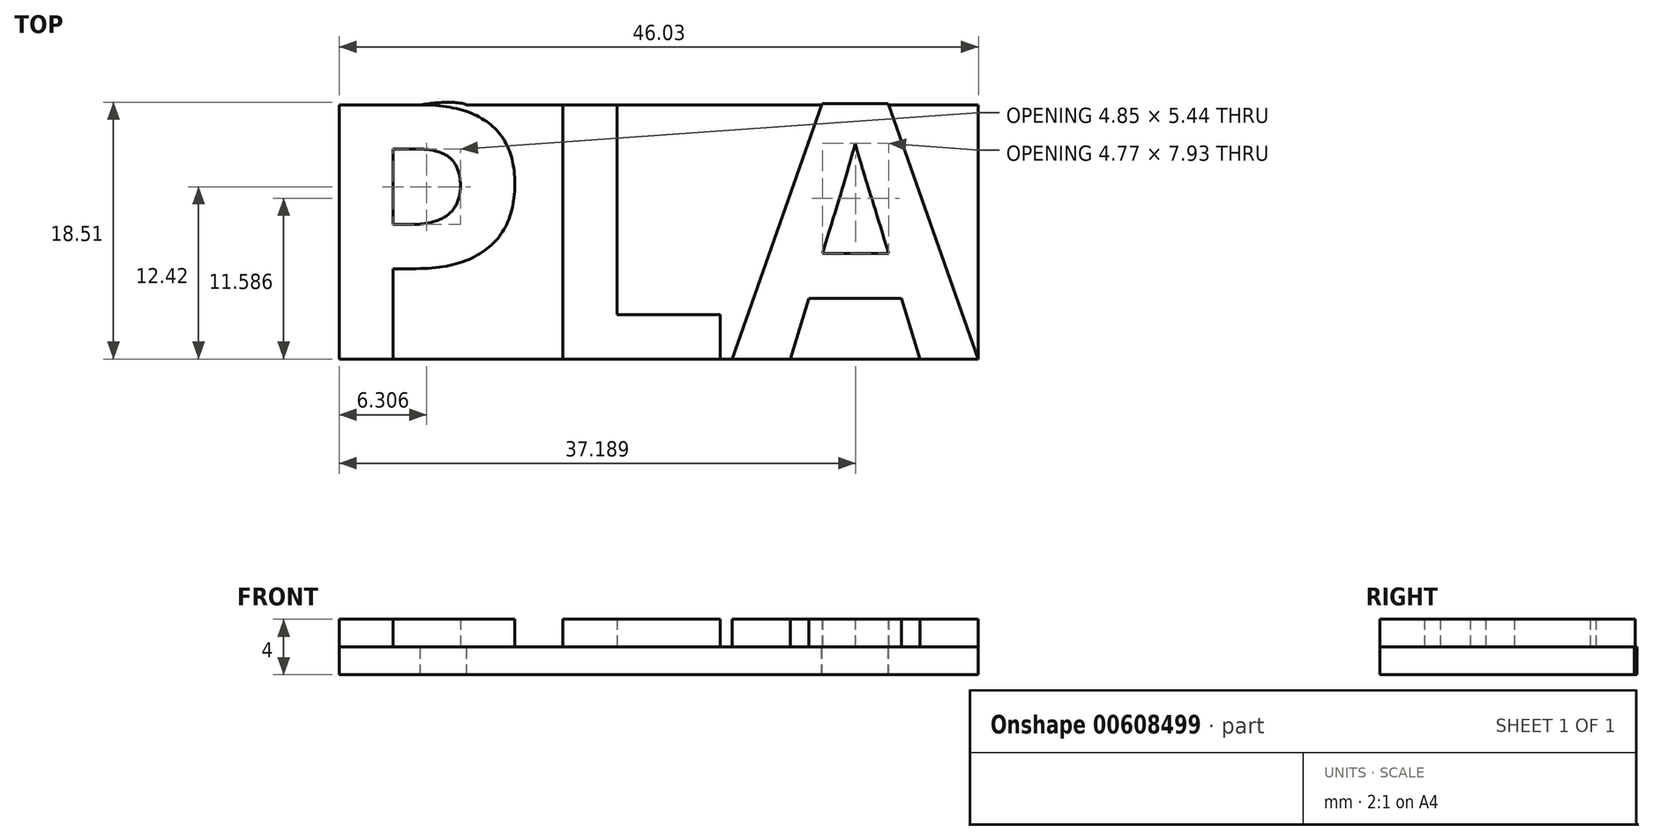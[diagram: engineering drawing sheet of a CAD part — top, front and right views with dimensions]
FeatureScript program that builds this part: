
annotation { "Feature Type Name" : "Feature", "Feature Type Description" : "" }
export const myFeature = defineFeature(function(context is Context, id is Id, definition is map)
    precondition{}
    {
        {
            var Q0;
            Q0=qCreatedBy(makeId("Top.planeOp"),FACE);
            var sketch = newSketch(context, id + "F0", { "sketchPlane" : qUnion([Q0])});
            skText(sketch, "E0", { "text": "PLA", "fontName": "OpenSans-Bold.ttf"});
            const initialGuessF0  = {"E0": [-0.025, 0, 1, 0, 0.01848]};
            skSetInitialGuess(sketch, initialGuessF0);
            skSolve(sketch);
        }
        {
            var Q0;
            Q0 = qSketchRegion(id + "F0", true);
            extrude(context, id + "F1", {"entities" : qUnion([Q0]), "depth" : 2 * mm, "offsetDistance" : 25 * mm});
        }
        {
            var Q0;
            Q0=qCreatedBy(makeId("Top.planeOp"),FACE);
            var sketch = newSketch(context, id + "F2", { "sketchPlane" : qUnion([Q0])});
            skFitSpline(sketch, "E1.0.0", {"points": [v(-11.77, 16.89) * mm, v(-10.04, 15.45) * mm, v(-10.04, 12.61) * mm]});
            skFitSpline(sketch, "E1.0.1", {"points": [v(-10.04, 12.61) * mm, v(-10.04, 9.65) * mm, v(-11.88, 8.08) * mm]});
            skFitSpline(sketch, "E1.0.2", {"points": [v(-11.88, 8.08) * mm, v(-13.73, 6.52) * mm, v(-17.14, 6.52) * mm]});
            skLineSegment(sketch, "E1.0.3", {"start": v(-17.14, 6.52) * mm, "end": v(-18.8, 6.52) * mm});
            skLineSegment(sketch, "E1.0.4", {"start": v(-18.8, 6.52) * mm, "end": v(-18.8, 0) * mm});
            skLineSegment(sketch, "E1.0.5", {"start": v(-18.8, 0) * mm, "end": v(-22.7, 0) * mm});
            skLineSegment(sketch, "E1.0.6", {"start": v(-22.7, 0) * mm, "end": v(-22.7, 18.33) * mm});
            skLineSegment(sketch, "E1.0.7", {"start": v(-22.7, 18.33) * mm, "end": v(-16.84, 18.33) * mm});
            skFitSpline(sketch, "E1.0.8", {"points": [v(-16.84, 18.33) * mm, v(-13.5, 18.33) * mm, v(-11.77, 16.89) * mm]});
            skLineSegment(sketch, "E1.1.0", {"start": v(4.74, 0) * mm, "end": v(-6.57, 0) * mm});
            skLineSegment(sketch, "E1.1.1", {"start": v(-6.57, 0) * mm, "end": v(-6.57, 18.33) * mm});
            skLineSegment(sketch, "E1.1.2", {"start": v(-6.57, 18.33) * mm, "end": v(-2.69, 18.33) * mm});
            skLineSegment(sketch, "E1.1.3", {"start": v(-2.69, 18.33) * mm, "end": v(-2.69, 3.2) * mm});
            skLineSegment(sketch, "E1.1.4", {"start": v(-2.69, 3.2) * mm, "end": v(4.74, 3.2) * mm});
            skLineSegment(sketch, "E1.1.5", {"start": v(4.74, 3.2) * mm, "end": v(4.74, 0) * mm});
            skLineSegment(sketch, "E1.2.0", {"start": v(23.34, 0) * mm, "end": v(19.15, 0) * mm});
            skLineSegment(sketch, "E1.2.1", {"start": v(19.15, 0) * mm, "end": v(17.82, 4.36) * mm});
            skLineSegment(sketch, "E1.2.2", {"start": v(17.82, 4.36) * mm, "end": v(11.14, 4.36) * mm});
            skLineSegment(sketch, "E1.2.3", {"start": v(11.14, 4.36) * mm, "end": v(9.81, 0) * mm});
            skLineSegment(sketch, "E1.2.4", {"start": v(9.81, 0) * mm, "end": v(5.62, 0) * mm});
            skLineSegment(sketch, "E1.2.5", {"start": v(5.62, 0) * mm, "end": v(12.1, 18.4) * mm});
            skLineSegment(sketch, "E1.2.6", {"start": v(12.1, 18.4) * mm, "end": v(16.84, 18.4) * mm});
            skLineSegment(sketch, "E1.2.7", {"start": v(16.84, 18.4) * mm, "end": v(23.34, 0) * mm});
            skLineSegment(sketch, "E2.bottom", {"start": v(23.34, 0) * mm, "end": v(-22.7, 0) * mm});
            skLineSegment(sketch, "E2.top", {"start": v(23.34, 18.33) * mm, "end": v(-22.7, 18.33) * mm});
            skLineSegment(sketch, "E2.left", {"start": v(23.34, 0) * mm, "end": v(23.34, 18.33) * mm});
            skSolve(sketch);
        }
        {
            var Q0;
            Q0 = qSketchRegion(id + "F2", true);
            extrude(context, id + "F3", {"entities" : qUnion([Q0]), "oppositeDirection" : true, "depth" : 2 * mm, "offsetDistance" : 25 * mm});
        }
    });
